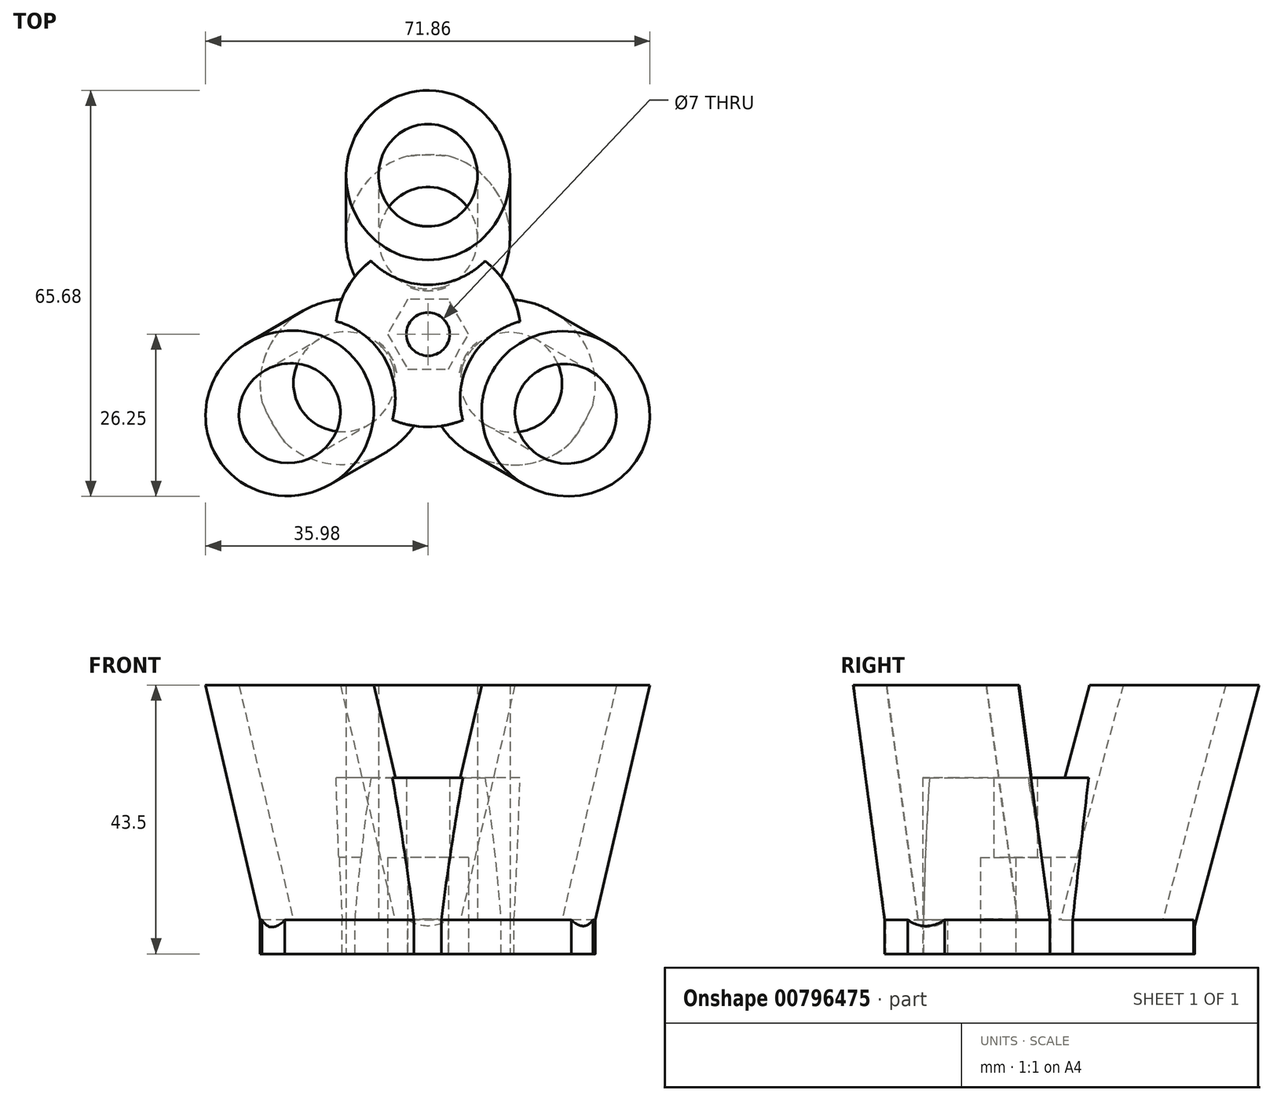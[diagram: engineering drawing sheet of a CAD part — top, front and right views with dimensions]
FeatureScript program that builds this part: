
annotation { "Feature Type Name" : "Feature", "Feature Type Description" : "" }
export const myFeature = defineFeature(function(context is Context, id is Id, definition is map)
    precondition{}
    {
        {
            var Q0;
            Q0=qCreatedBy(makeId("Top.planeOp"),FACE);
            var sketch = newSketch(context, id + "F0", { "sketchPlane" : qUnion([Q0])});
            skCircle(sketch, "E0", {"center": v(0, 0) * mm, "radius": 15 * mm});
            skLineSegment(sketch, "E1", {"start": v(0, 0) * mm, "end": v(0, 56.02) * mm});
            skLineSegment(sketch, "E2", {"start": v(0, 0) * mm, "end": v(54.27, -31.33) * mm});
            skLineSegment(sketch, "E3", {"start": v(0, 0) * mm, "end": v(-44.73, -25.83) * mm});
            skCircle(sketch, "E4", {"center": v(13, -7.5) * mm, "radius": 8 * mm});
            skCircle(sketch, "E5", {"center": v(-13, -7.5) * mm, "radius": 8 * mm});
            skCircle(sketch, "E6", {"center": v(0, 15) * mm, "radius": 8 * mm});
            skLineSegment(sketch, "E7", {"start": v(13, -7.5) * mm, "end": v(-5.61, -39.72) * mm});
            skLineSegment(sketch, "E8", {"start": v(-13, -7.5) * mm, "end": v(-29.84, 21.68) * mm});
            skLineSegment(sketch, "E9", {"start": v(0, 15) * mm, "end": v(16.9, 15) * mm});
            skSolve(sketch);
        }
        {
            var Q0;
            Q0=qCreatedBy(makeId("Top.planeOp"),FACE);
            var Q1;
            Q1=sQuery(id+"F0.wireOp",EDGE,"E8");
            cPlane(context, id + "F1", {"entities" : qUnion([Q0, Q1]), "cplaneType" : CPlaneType.LINE_ANGLE, "offset" : 25 * mm, "angle" : 15 * degree, "oppositeDirection" : true, "width" : 150 * mm, "height" : 150 * mm});
        }
        {
            var Q0;
            Q0=qCreatedBy(makeId("Top.planeOp"),FACE);
            var Q1;
            Q1=sQuery(id+"F0.wireOp",EDGE,"E7");
            cPlane(context, id + "F2", {"entities" : qUnion([Q0, Q1]), "cplaneType" : CPlaneType.LINE_ANGLE, "offset" : 25 * mm, "angle" : 15 * degree, "oppositeDirection" : true, "width" : 150 * mm, "height" : 150 * mm});
        }
        {
            var Q0;
            Q0=qCreatedBy(makeId("Top.planeOp"),FACE);
            var Q1;
            Q1=sQuery(id+"F0.wireOp",EDGE,"E9");
            cPlane(context, id + "F3", {"entities" : qUnion([Q0, Q1]), "cplaneType" : CPlaneType.LINE_ANGLE, "offset" : 25 * mm, "angle" : 15 * degree, "oppositeDirection" : true, "width" : 150 * mm, "height" : 150 * mm});
        }
        {
            var Q0;
            Q0=qCreatedBy(id+"F1.planeOp",FACE);
            var sketch = newSketch(context, id + "F4", { "sketchPlane" : qUnion([Q0])});
            skCircle(sketch, "E10", {"center": v(-12.54, 7.37) * mm, "radius": 8 * mm});
            skCircle(sketch, "E11", {"center": v(-12.54, 7.37) * mm, "radius": 13.25 * mm});
            skSolve(sketch);
        }
        {
            var Q0;
            Q0=qCreatedBy(id+"F2.planeOp",FACE);
            var sketch = newSketch(context, id + "F5", { "sketchPlane" : qUnion([Q0])});
            skCircle(sketch, "E12", {"center": v(12.44, 7.45) * mm, "radius": 8 * mm});
            skCircle(sketch, "E13", {"center": v(12.44, 7.45) * mm, "radius": 13.25 * mm});
            skSolve(sketch);
        }
        {
            var Q0;
            Q0=qCreatedBy(id+"F3.planeOp",FACE);
            var sketch = newSketch(context, id + "F6", { "sketchPlane" : qUnion([Q0])});
            skCircle(sketch, "E14", {"center": v(0, -14.48) * mm, "radius": 8 * mm});
            skCircle(sketch, "E15", {"center": v(0, -14.48) * mm, "radius": 13.25 * mm});
            skSolve(sketch);
        }
        {
            var Q0;
            Q0=makeQuery(id+"F5.imprint","IMPRINT",FACE,{"disambiguationData":[TD([[makeQuery(id+"F5.imprint","IMPRINT",EDGE,{"derivedFrom":sQuery(id+"F5.wireOp",EDGE,"E12")}),-1.0]])]});
            extrude(context, id + "F7", {"entities" : qUnion([Q0]), "oppositeDirection" : true, "depth" : 50 * mm, "offsetDistance" : 25 * mm});
        }
        {
            var Q0;
            Q0 = qSketchRegion(id + "F4", true);
            extrude(context, id + "F8", {"entities" : qUnion([Q0]), "oppositeDirection" : true, "depth" : 50 * mm, "offsetDistance" : 25 * mm});
        }
        {
            var Q0;
            Q0 = qSketchRegion(id + "F6", true);
            extrude(context, id + "F9", {"entities" : qUnion([Q0]), "oppositeDirection" : true, "depth" : 50 * mm, "offsetDistance" : 25 * mm});
        }
        {
            var Q0;
            {var subQ5=sQuery(id+"F0.wireOp",EDGE,"E6");var subQ7=sQuery(id+"F0.wireOp",EDGE,"E0");var subQ8=makeQuery(id+"F0.imprint","INTERSECT",VERTEX,{"disambiguationData":[OD(0.0)],"derivedFrom":[subQ7,subQ5]});Q0=makeQuery(id+"F0.imprint","IMPRINT",FACE,{"disambiguationData":[TD([[makeQuery(id+"F0.imprint","IMPRINT",EDGE,{"disambiguationData":[TD([[subQ8,1.0]])],"derivedFrom":subQ7}),1.0]])]});}
            var Q1;
            {var subQ1=sQuery(id+"F0.wireOp",EDGE,"E0");var subQ7=sQuery(id+"F0.wireOp",EDGE,"E6");var subQ9=makeQuery(id+"F0.imprint","INTERSECT",VERTEX,{"disambiguationData":[OD(1.0)],"derivedFrom":[subQ1,subQ7]});Q1=makeQuery(id+"F0.imprint","IMPRINT",FACE,{"disambiguationData":[TD([[makeQuery(id+"F0.imprint","IMPRINT",EDGE,{"disambiguationData":[TD([[subQ9,-1.0]])],"derivedFrom":subQ1}),1.0]])]});}
            var Q2;
            {var subQ1=sQuery(id+"F0.wireOp",EDGE,"E0");var subQ7=sQuery(id+"F0.wireOp",EDGE,"E5");var subQ9=makeQuery(id+"F0.imprint","INTERSECT",VERTEX,{"disambiguationData":[OD(1.0)],"derivedFrom":[subQ1,subQ7]});Q2=makeQuery(id+"F0.imprint","IMPRINT",FACE,{"disambiguationData":[TD([[makeQuery(id+"F0.imprint","IMPRINT",EDGE,{"disambiguationData":[TD([[subQ9,-1.0]])],"derivedFrom":subQ1}),1.0]])]});}
            extrude(context, id + "F10", {"entities" : qUnion([Q0, Q1, Q2]), "depth" : 25 * mm, "offsetDistance" : 25 * mm});
        }
        {
            var Q0;
            Q0=qCreatedBy(makeId("Top.planeOp"),FACE);
            var sketch = newSketch(context, id + "F11", { "sketchPlane" : qUnion([Q0])});
            skCircle(sketch, "E16", {"center": v(0, 0) * mm, "radius": 29 * mm});
            skSolve(sketch);
        }
        {
            var Q0;
            Q0 = qSketchRegion(id + "F11", true);
            extrude(context, id + "F12", {"entities" : qUnion([Q0]), "oppositeDirection" : true, "depth" : 3.5 * mm, "offsetDistance" : 25 * mm, "hasSecondDirection" : true, "secondDirectionOppositeDirection" : false, "secondDirectionDepth" : 2 * mm});
        }
        {
            var Q0;
            Q0=qCreatedBy(makeId("Top.planeOp"),FACE);
            var sketch = newSketch(context, id + "F13", { "sketchPlane" : qUnion([Q0])});
            skCircle(sketch, "E17", {"center": v(0, 0) * mm, "radius": 3.5 * mm});
            skSolve(sketch);
        }
        {
            var Q0;
            Q0 = qSketchRegion(id + "F13", true);
            extrude(context, id + "F14", {"entities" : qUnion([Q0]), "operationType" : NewBodyOperationType.REMOVE, "endBound" : BoundingType.THROUGH_ALL, "depth" : 25 * mm, "offsetDistance" : 25 * mm, "hasSecondDirection" : true, "secondDirectionOppositeDirection" : true, "secondDirectionDepth" : 25 * mm});
        }
        {
            var Q0;
            Q0=makeQuery(id+"F7.opExtrude","SWEPT_BODY",BODY,{"disambiguationData":[OSD([sQuery(id+"F5.wireOp",EDGE,"E12"),sQuery(id+"F5.wireOp",EDGE,"E13")])]});
            var Q1;
            Q1=makeQuery(id+"F8.opExtrude","SWEPT_BODY",BODY,{"disambiguationData":[OSD([sQuery(id+"F4.wireOp",EDGE,"E10"),sQuery(id+"F4.wireOp",EDGE,"E11")])]});
            var Q2;
            Q2=makeQuery(id+"F9.opExtrude","SWEPT_BODY",BODY,{"disambiguationData":[OSD([sQuery(id+"F6.wireOp",EDGE,"E14"),sQuery(id+"F6.wireOp",EDGE,"E15")])]});
            var Q3;
            Q3=makeQuery(id+"F10.opExtrude","SWEPT_BODY",BODY,{"disambiguationData":[OSD([sQuery(id+"F0.wireOp",EDGE,"E0"),sQuery(id+"F0.wireOp",EDGE,"E4"),sQuery(id+"F0.wireOp",EDGE,"E5"),sQuery(id+"F0.wireOp",EDGE,"E6")])]});
            var Q4;
            Q4=makeQuery(id+"F12.opExtrude","SWEPT_BODY",BODY,{"disambiguationData":[OSD([sQuery(id+"F11.wireOp",EDGE,"E16")])]});
            booleanBodies(context, id + "F15", {"operationType" : BooleanOperationType.UNION, "tools" : qUnion([Q0, Q1, Q2, Q3, Q4])});
        }
        {
            var Q0;
            Q0=makeQuery(id+"F12.opExtrude","CAP_FACE",FACE,{"disambiguationData":[OSD([sQuery(id+"F11.wireOp",EDGE,"E16")])],"isStart":false});
            var sketch = newSketch(context, id + "F16", { "sketchPlane" : qUnion([Q0])});
            skCircle(sketch, "E18.cCircle", {"center": v(0, 0) * mm, "radius": 5.67 * mm, "construction": true});
            skLineSegment(sketch, "E18.0", {"start": v(3.28, -5.67) * mm, "end": v(-3.28, -5.67) * mm});
            skLineSegment(sketch, "E18.1", {"start": v(-3.28, -5.67) * mm, "end": v(-6.55, 0) * mm});
            skLineSegment(sketch, "E18.2", {"start": v(-6.55, 0) * mm, "end": v(-3.27, 5.67) * mm});
            skLineSegment(sketch, "E18.3", {"start": v(-3.28, 5.67) * mm, "end": v(3.27, 5.67) * mm});
            skLineSegment(sketch, "E18.4", {"start": v(3.27, 5.67) * mm, "end": v(6.55, 0) * mm});
            skLineSegment(sketch, "E18.5", {"start": v(6.55, 0) * mm, "end": v(3.27, -5.67) * mm});
            skPoint(sketch, "E18.0.midPoint", {"position": v(0, -5.67) * mm});
            skSolve(sketch);
        }
        {
            var Q0;
            Q0 = qSketchRegion(id + "F16", true);
            extrude(context, id + "F17", {"entities" : qUnion([Q0]), "operationType" : NewBodyOperationType.REMOVE, "oppositeDirection" : true, "depth" : 20 * mm, "offsetDistance" : 25 * mm});
        }
        {
            var Q0;
            Q0=makeQuery(id+"F10.opExtrude","CAP_FACE",FACE,{"disambiguationData":[OSD([sQuery(id+"F0.wireOp",EDGE,"E0"),sQuery(id+"F0.wireOp",EDGE,"E4"),sQuery(id+"F0.wireOp",EDGE,"E5"),sQuery(id+"F0.wireOp",EDGE,"E6")])],"isStart":false});
            var sketch = newSketch(context, id + "F18", { "sketchPlane" : qUnion([Q0])});
            skArc(sketch, "E19", {"start": v(-9.21, 11.84) * mm, "mid": v(0, 7.99) * mm, "end": v(9.21, 11.84) * mm});
            skArc(sketch, "E20", {"start": v(14.86, 2.04) * mm, "mid": v(13, 7.49) * mm, "end": v(9.21, 11.84) * mm});
            skArc(sketch, "E21", {"start": v(14.86, 2.04) * mm, "mid": v(6.93, -4) * mm, "end": v(5.65, -13.9) * mm});
            skArc(sketch, "E22", {"start": v(-5.76, -13.85) * mm, "mid": v(-0.06, -15) * mm, "end": v(5.65, -13.9) * mm});
            skArc(sketch, "E23", {"start": v(-5.76, -13.85) * mm, "mid": v(-7, -3.99) * mm, "end": v(-14.85, 2.1) * mm});
            skArc(sketch, "E24", {"start": v(-9.21, 11.84) * mm, "mid": v(-13.04, 7.55) * mm, "end": v(-14.85, 2.1) * mm});
            skCircle(sketch, "E25", {"center": v(0, 0) * mm, "radius": 3.5 * mm});
            skPoint(sketch, "E25.first.point", {"position": v(0.88, 3.39) * mm});
            skPoint(sketch, "E25.second.point", {"position": v(-3.5, 0) * mm});
            skPoint(sketch, "E25.third.point", {"position": v(2.81, -2.08) * mm});
            skSolve(sketch);
        }
        {
            var Q0;
            Q0 = qSketchRegion(id + "F18", true);
            extrude(context, id + "F19", {"entities" : qUnion([Q0]), "operationType" : NewBodyOperationType.ADD, "oppositeDirection" : true, "depth" : 12.9 * mm, "offsetDistance" : 25 * mm});
        }
        {
            var Q0;
            {var subQ0=sQuery(id+"F0.wireOp",EDGE,"E0");var subQ1=sQuery(id+"F11.wireOp",EDGE,"E16");Q0=makeQuery(id+"F15.opBoolean","SPLIT",FACE,{"disambiguationData":[TD([makeQuery(id+"F10.opExtrude","SWEPT_FACE",FACE,{"disambiguationData":[OSD([subQ0]),TDD([makeQuery(id+"F0.imprint","IMPRINT",EDGE,{"disambiguationData":[TD([[makeQuery(id+"F0.imprint","INTERSECT",VERTEX,{"disambiguationData":[OD(1.0)],"derivedFrom":[subQ0,sQuery(id+"F0.wireOp",EDGE,"E5")]}),-1.0]])],"derivedFrom":subQ0})])]})])],"derivedFrom":makeQuery(id+"F12.opExtrude","CAP_FACE",FACE,{"disambiguationData":[OSD([subQ1])],"isStart":true})});}
            var Q1;
            {var subQ0=sQuery(id+"F0.wireOp",EDGE,"E0");var subQ1=sQuery(id+"F11.wireOp",EDGE,"E16");Q1=makeQuery(id+"F15.opBoolean","SPLIT",FACE,{"disambiguationData":[TD([makeQuery(id+"F10.opExtrude","SWEPT_FACE",FACE,{"disambiguationData":[OSD([subQ0]),TDD([makeQuery(id+"F0.imprint","IMPRINT",EDGE,{"disambiguationData":[TD([[makeQuery(id+"F0.imprint","INTERSECT",VERTEX,{"disambiguationData":[OD(0.0)],"derivedFrom":[subQ0,sQuery(id+"F0.wireOp",EDGE,"E6")]}),1.0]])],"derivedFrom":subQ0})])]})])],"derivedFrom":makeQuery(id+"F12.opExtrude","CAP_FACE",FACE,{"disambiguationData":[OSD([subQ1])],"isStart":true})});}
            var Q2;
            {var subQ0=sQuery(id+"F0.wireOp",EDGE,"E0");var subQ1=sQuery(id+"F11.wireOp",EDGE,"E16");Q2=makeQuery(id+"F15.opBoolean","SPLIT",FACE,{"disambiguationData":[TD([makeQuery(id+"F10.opExtrude","SWEPT_FACE",FACE,{"disambiguationData":[OSD([subQ0]),TDD([makeQuery(id+"F0.imprint","IMPRINT",EDGE,{"disambiguationData":[TD([[makeQuery(id+"F0.imprint","INTERSECT",VERTEX,{"disambiguationData":[OD(1.0)],"derivedFrom":[subQ0,sQuery(id+"F0.wireOp",EDGE,"E6")]}),-1.0]])],"derivedFrom":subQ0})])]})])],"derivedFrom":makeQuery(id+"F12.opExtrude","CAP_FACE",FACE,{"disambiguationData":[OSD([subQ1])],"isStart":true})});}
            extrude(context, id + "F20", {"entities" : qUnion([Q0, Q1, Q2]), "operationType" : NewBodyOperationType.REMOVE, "oppositeDirection" : true, "depth" : 25 * mm, "offsetDistance" : 25 * mm});
        }
        {
            var Q0;
            Q0=qCreatedBy(makeId("Top.planeOp"),FACE);
            cPlane(context, id + "F21", {"entities" : qUnion([Q0]), "cplaneType" : CPlaneType.OFFSET, "offset" : 40 * mm, "width" : 150 * mm, "height" : 150 * mm});
        }
        {
            var Q0;
            Q0=qCreatedBy(id+"F21.planeOp",FACE);
            var sketch = newSketch(context, id + "F22", { "sketchPlane" : qUnion([Q0])});
            skLineSegment(sketch, "E26.bottom", {"start": v(-54.21, 41.83) * mm, "end": v(56.15, 41.83) * mm});
            skLineSegment(sketch, "E26.top", {"start": v(-54.21, -36.49) * mm, "end": v(56.15, -36.49) * mm});
            skLineSegment(sketch, "E26.left", {"start": v(-54.21, 41.83) * mm, "end": v(-54.21, -36.49) * mm});
            skLineSegment(sketch, "E26.right", {"start": v(56.15, 41.83) * mm, "end": v(56.15, -36.49) * mm});
            skSolve(sketch);
        }
        {
            var Q0;
            Q0 = qSketchRegion(id + "F22", true);
            extrude(context, id + "F23", {"entities" : qUnion([Q0]), "operationType" : NewBodyOperationType.REMOVE, "depth" : 25 * mm, "offsetDistance" : 25 * mm});
        }
    });
